# Revit family: СигнализаторЗагазованностиПульсар_R19ЭлОборуд
name_source: partatom
category: Арматура трубопроводов
units: mm (PartAtom-declared; Revit-internal decimal feet)

## family parameters
Всегда вертикально = Да
Заголовок OmniClass = Distribution Boards and Control Panels
На основе рабочей плоскости = Нет
Номер OmniClass = 23.80.30.11.17
Общий = Нет
При загрузке вырезать с полостями = Нет
Размер круглого соединителя = Использовать диаметр
Тип детали = Нормальный

## types (28) — shared parameters
ADSK_Единица измерения = шт.
ADSK_Завод-изготовитель = Пульсар
ADSK_Размер_Высота = 92 мм
ADSK_Размер_Глубина = 29 мм
ADSK_Размер_Ширина = 92 мм
Время установления рабочего режима = не более 30 с
Масса = не более 0,15 кг
Материал = <По категории>
Наличие источника питания = источник питания в комплекте
Потребляемая мощность = не более 1,0 (1,0) В,А (Вт)
Средний срок службы = 10 лет
Средняя наработка до отказа = 30000 часов
Температура окружающей среды = -10 до +45 °С
zero-valued in all types: ADSK_Масса

## per-type parameters (varying)
| type | ADSK_Наименование | Время срабатывания сигнализации для исполнения «Пульсар» СO | Время срабатывания сигнализации для исполнения «Пульсар» СН | Ду | Наличие клапана | Параметры электрического питания без адаптера питания — от внешнего источника постоянного тока | Параметры электрического питания с адаптером питания от сети переменного тока с частотой (50±1) Гц |
| Сигнализатор загазованности «Пульсар» CH с клапаном Ду32 | Сигнализатор загазованности «Пульсар» CH с клапаном Ду32 |  | не более 15 с | 32 мм | с клапаном |  | 220±23В |
| Сигнализатор загазованности «Пульсар» CH с латунным клапаном Ду20 | Сигнализатор загазованности «Пульсар» CH с латунным клапаном Ду20 |  | не более 15 с | 20 мм | с клапаном |  | 220±23В |
| Сигнализатор загазованности «Пульсар» CH с латунным клапаном Ду25 | Сигнализатор загазованности «Пульсар» CH с латунным клапаном Ду25 |  | не более 15 с | 25 мм | с клапаном |  | 220±23В |
| Сигнализатор загазованности «Пульсар» CH с клапаном Ду20 | Сигнализатор загазованности «Пульсар» CH с клапаном Ду20 |  | не более 15 с | 20 мм | с клапаном |  | 220±23В |
| Сигнализатор загазованности «Пульсар» CH с клапаном Ду25 | Сигнализатор загазованности «Пульсар» CH с клапаном Ду25 |  | не более 15 с | 25 мм | с клапаном |  | 220±23В |
| Сигнализатор загазованности «Пульсар» CO с соединительным кабелем | Сигнализатор загазованности «Пульсар» CO с соединительным кабелем | не более 60 с |  | 25 мм | без клапана | 12±0,2В |  |
| Сигнализатор загазованности «Пульсар» CH с источником питания | Сигнализатор загазованности «Пульсар» CH с источником питания |  | не более 15 с | 25 мм | без клапана |  | 220±23В |
| Сигнализатор загазованности «Пульсар» CO, температура эксплуатации +5 до +45 °C | Сигнализатор загазованности «Пульсар» CO, температура эксплуатации +5 до +45 °C | не более 60 с |  | 25 мм | без клапана | 12±0,2В |  |
| Сигнализатор загазованности «Пульсар» CH с латунным клапаном Ду15 | Сигнализатор загазованности «Пульсар» CH с латунным клапаном Ду15 |  | не более 15 с | 15 мм | с клапаном |  | 220±23В |
| Сигнализатор загазованности «Пульсар» CH с латунным клапаном Ду32 | Сигнализатор загазованности «Пульсар» CH с латунным клапаном Ду32 |  | не более 15 с | 32 мм | с клапаном |  | 220±23В |
| Сигнализатор загазованности «Пульсар» CH с клапаном Ду15 | Сигнализатор загазованности «Пульсар» CH с клапаном Ду15 |  | не более 15 с | 15 мм | с клапаном |  | 220±23В |
| Сигнализатор загазованности «Пульсар» 2CO-2CH c клапаном Ду25 | Сигнализатор загазованности «Пульсар» CH с клапаном Ду15 | не более 60 с | не более 15 с | 25 мм | с клапаном |  | 220±23В |
| Сигнализатор загазованности «Пульсар» CO-CH энергозависимый c клапаном Ду25 | Сигнализатор загазованности «Пульсар» CO-CH энергозависимый c клапаном Ду25 | не более 60 с | не более 15 с | 25 мм | с клапаном |  | 220±23В |
| Сигнализатор загазованности «Пульсар» 2CO-2CH c клапаном Ду32 | Сигнализатор загазованности «Пульсар» 2CO-2CH c клапаном Ду32 | не более 60 с | не более 15 с | 32 мм | с клапаном |  | 220±23В |
| Сигнализатор загазованности «Пульсар» CO-CH c клапаном Ду25 | Сигнализатор загазованности «Пульсар» CO-CH c клапаном Ду25 | не более 60 с | не более 15 с | 25 мм | с клапаном |  | 220±23В |
| Сигнализатор загазованности «Пульсар» CO-CH без клапана | Сигнализатор загазованности «Пульсар» CO-CH без клапана | не более 60 с | не более 15 с | 25 мм | с клапаном |  | 220±23В |
| Сигнализатор загазованности «Пульсар» 2CO-2CH c клапаном Ду15 | Сигнализатор загазованности «Пульсар» 2CO-2CH c клапаном Ду15 | не более 60 с | не более 15 с | 15 мм | с клапаном |  | 220±23В |
| Сигнализатор загазованности «Пульсар» 2CO-2CH c клапаном Ду20 | Сигнализатор загазованности «Пульсар» 2CO-2CH c клапаном Ду20 | не более 60 с | не более 15 с | 20 мм | с клапаном |  | 220±23В |
| Сигнализатор загазованности «Пульсар» CO-CH c латунным клапаном Ду25 | Сигнализатор загазованности «Пульсар» CO-CH c латунным клапаном Ду25 | не более 60 с | не более 15 с | 25 мм | с клапаном |  | 220±23В |
| Сигнализатор загазованности «Пульсар» CO-CH c латунным клапаном Ду32 | Сигнализатор загазованности «Пульсар» CO-CH c латунным клапаном Ду32 | не более 60 с | не более 15 с | 32 мм | с клапаном |  | 220±23В |
| Сигнализатор загазованности «Пульсар» CO-CH c клапаном Ду15 | Сигнализатор загазованности «Пульсар» CO-CH c клапаном Ду15 | не более 60 с | не более 15 с | 15 мм | с клапаном |  | 220±23В |
| Сигнализатор загазованности «Пульсар» CO-CH c клапаном Ду20 | Сигнализатор загазованности «Пульсар» CO-CH c клапаном Ду20 | не более 60 с | не более 15 с | 20 мм | с клапаном |  | 220±23В |
| Сигнализатор загазованности «Пульсар» CO-CH энергозависимый c клапаном Ду20 | Сигнализатор загазованности «Пульсар» CO-CH энергозависимый c клапаном Ду20 | не более 60 с | не более 15 с | 20 мм | с клапаном |  | 220±23В |
| Сигнализатор загазованности «Пульсар» CO-CH энергозависимый c клапаном Ду32 | Сигнализатор загазованности «Пульсар» CO-CH энергозависимый c клапаном Ду32 | не более 60 с | не более 15 с | 32 мм | с клапаном |  | 220±23В |
| Сигнализатор загазованности «Пульсар» CO-CH c клапаном Ду32 | Сигнализатор загазованности «Пульсар» CO-CH c клапаном Ду32 | не более 60 с | не более 15 с | 32 мм | с клапаном |  | 220±23В |
| Сигнализатор загазованности «Пульсар» CO-CH c латунным клапаном Ду20 | Сигнализатор загазованности «Пульсар» CO-CH c латунным клапаном Ду20 | не более 60 с | не более 15 с | 20 мм | с клапаном |  | 220±23В |
| Сигнализатор загазованности «Пульсар» CO-CH c латунным клапаном Ду15 | Сигнализатор загазованности «Пульсар» CO-CH c латунным клапаном Ду15 | не более 60 с | не более 15 с | 15 мм | с клапаном |  | 220±23В |
| Сигнализатор загазованности «Пульсар» CO-CH энергозависимый c клапаном Ду15 | Сигнализатор загазованности «Пульсар» CO-CH энергозависимый c клапаном Ду15 | не более 60 с | не более 15 с | 15 мм | с клапаном |  | 220±23В |
